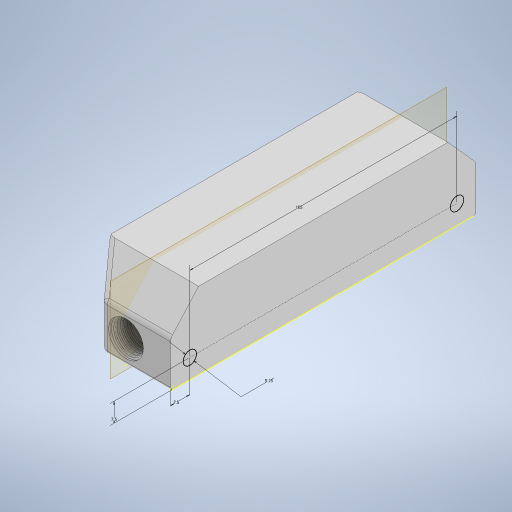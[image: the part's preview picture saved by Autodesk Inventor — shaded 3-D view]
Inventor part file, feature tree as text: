
AUTODESK INVENTOR PART (.ipt)
format: ipt  version: 2023 (Build 270158000, 158)  size: 549,376 bytes
history: native  units: mm
features: sketch x11, extrude x8, plane x3, fillet x2, projected_geometry x2, helix x1, mirror x1, other x1
ambient origin geometry x8: Origin, YZ Plane, XZ Plane, XY Plane, X Axis, Y Axis, Z Axis, Center Point
bodies: Solid1 (feature_tree)
feature tree (29):
  extrude  "Extrusion1"  Depth=35.0mm
  extrude  "Extrusion2"  Depth=30.0mm
  plane  "Work Plane4"
  helix  "Coil1"  [1 undecoded]
  extrude  "Extrusion3"  Depth=1.0mm
  plane  "Work Plane1"
  extrude  "Extrusion4"  Depth=11.0mm
  extrude  "Extrusion5"  Depth=2.0mm TaperAngle=0.0deg
  extrude  "Extrusion6"  Depth=2.0mm
  extrude  "Extrusion11"  Depth=3.0mm
  mirror  "Mirror1"
  fillet  "Fillet2"  [1 undecoded]
  fillet  "Fillet3"  Radius=3.0mm
  sketch  "Sketch13"  dims[d45=90.0deg d46=1.337mm d47=53.75mm d48=20.0mm d49=0.0mm d50=90.0deg d51=90.0deg d52=0.0mm d53=0.0mm]
  extrude  "Extrusion12"  Depth=9.599311mm
  plane  "Work Plane5"
  sketch  "Sketch15"  dims[d56=105.0mm d58=7.5mm d59=5.25mm d60=7.5mm d61=1.0mm d62=0.0mm]
  sketch  "Sketch1"  dims[d0=120.0mm d1=35.0mm]
  sketch  "Sketch2"  dims[d2=30.0mm d3=0.0mm d4=8.919358mm d5=13.65mm]
  sketch  "Sketch3"  dims[d6=30.0mm d7=0.0mm d10=1.0mm]
  sketch  "Sketch4"  dims[d11=29.0mm d12=0.0mm d14=11.0mm]
  projected_geometry  "Projected Loop1"
  sketch  "Sketch5"  dims[d15=5.0mm d16=2.0mm d17=0.0mm]
  sketch  "Sketch6"  dims[d18=2.0mm d19=2.0mm]
  sketch  "Sketch11"  dims[d20=0.0mm d21=0.0mm d22=17.65mm d23=0.0mm d24=0.0mm d25=3.0mm]
  other  "Work Axis2"
  sketch  "Sketch12"  dims[d26=1.0mm d42=9.599311mm d43=1.15mm d44=0.3mm]
  sketch  "Sketch14"  dims[d54=10.0mm d55=0.0mm]
  projected_geometry  "Projected Loop2"
note: 2 required parameter values undecoded (feature->parameter linkage not recoverable at this tier; creation-order binding heuristic only, values carry confidence <= 0.55)
